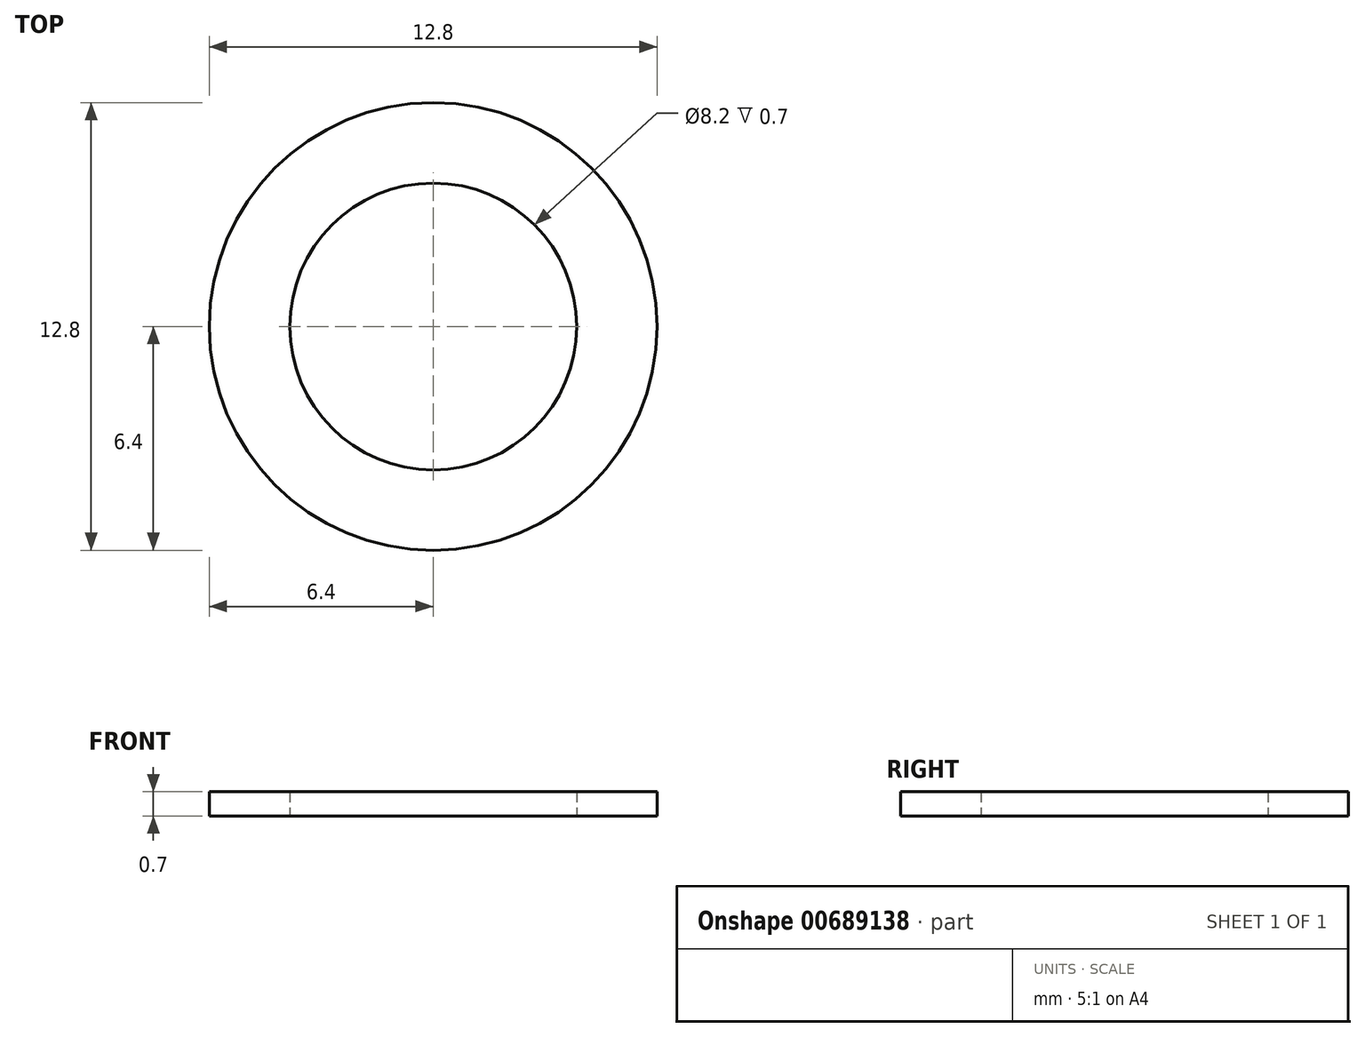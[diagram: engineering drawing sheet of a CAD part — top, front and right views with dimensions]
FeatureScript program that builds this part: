
annotation { "Feature Type Name" : "Feature", "Feature Type Description" : "" }
export const myFeature = defineFeature(function(context is Context, id is Id, definition is map)
    precondition{}
    {
        {
            var Q0;
            Q0=qCreatedBy(makeId("Top.planeOp"),FACE);
            var sketch = newSketch(context, id + "F0", { "sketchPlane" : qUnion([Q0])});
            skCircle(sketch, "E0", {"center": v(0, 0) * mm, "radius": 6.4 * mm});
            skCircle(sketch, "E1", {"center": v(0, 0) * mm, "radius": 4.1 * mm});
            skSolve(sketch);
        }
        {
            var Q0;
            Q0 = qSketchRegion(id + "F0", true);
            extrude(context, id + "F1", {"entities" : qUnion([Q0]), "depth" : 0.7 * mm, "offsetDistance" : 25 * mm});
        }
    });
